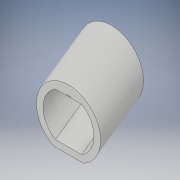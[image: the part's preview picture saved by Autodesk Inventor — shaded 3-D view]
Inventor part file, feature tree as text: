
AUTODESK INVENTOR PART (.ipt)
format: ipt  version: 2017 (Build 210142000, 142)  size: 145,920 bytes
history: native  units: in
note: dims shown in document units (in); Inventor stores cm internally (conversion verified against a paired STEP export)
features: sketch x2, other x1, plane x1, sweep x1
ambient origin geometry x8: Origin, YZ Plane, XZ Plane, XY Plane, X Axis, Y Axis, Z Axis, Center Point
bodies: Solid1 (feature_tree), Solid2 (feature_tree)
feature tree (5):
  other  "ramp"
  sketch  "Sketch1"  dims[d1=4.0in d2=1.0in d28=8.0in]
  plane  "Work Plane2"
  sketch  "Sketch6"  dims[d29=0.3779in d30=0.0in d31=0.0in d34=0.5833in d35=0.0625in d36=0.0625in d37=0.25in d38=0.125in d39=45.0deg d40=0.0892in d41=0.0884in d42=0.125in d43=0.0in d44=0.0in]
  sweep  "light angle"
